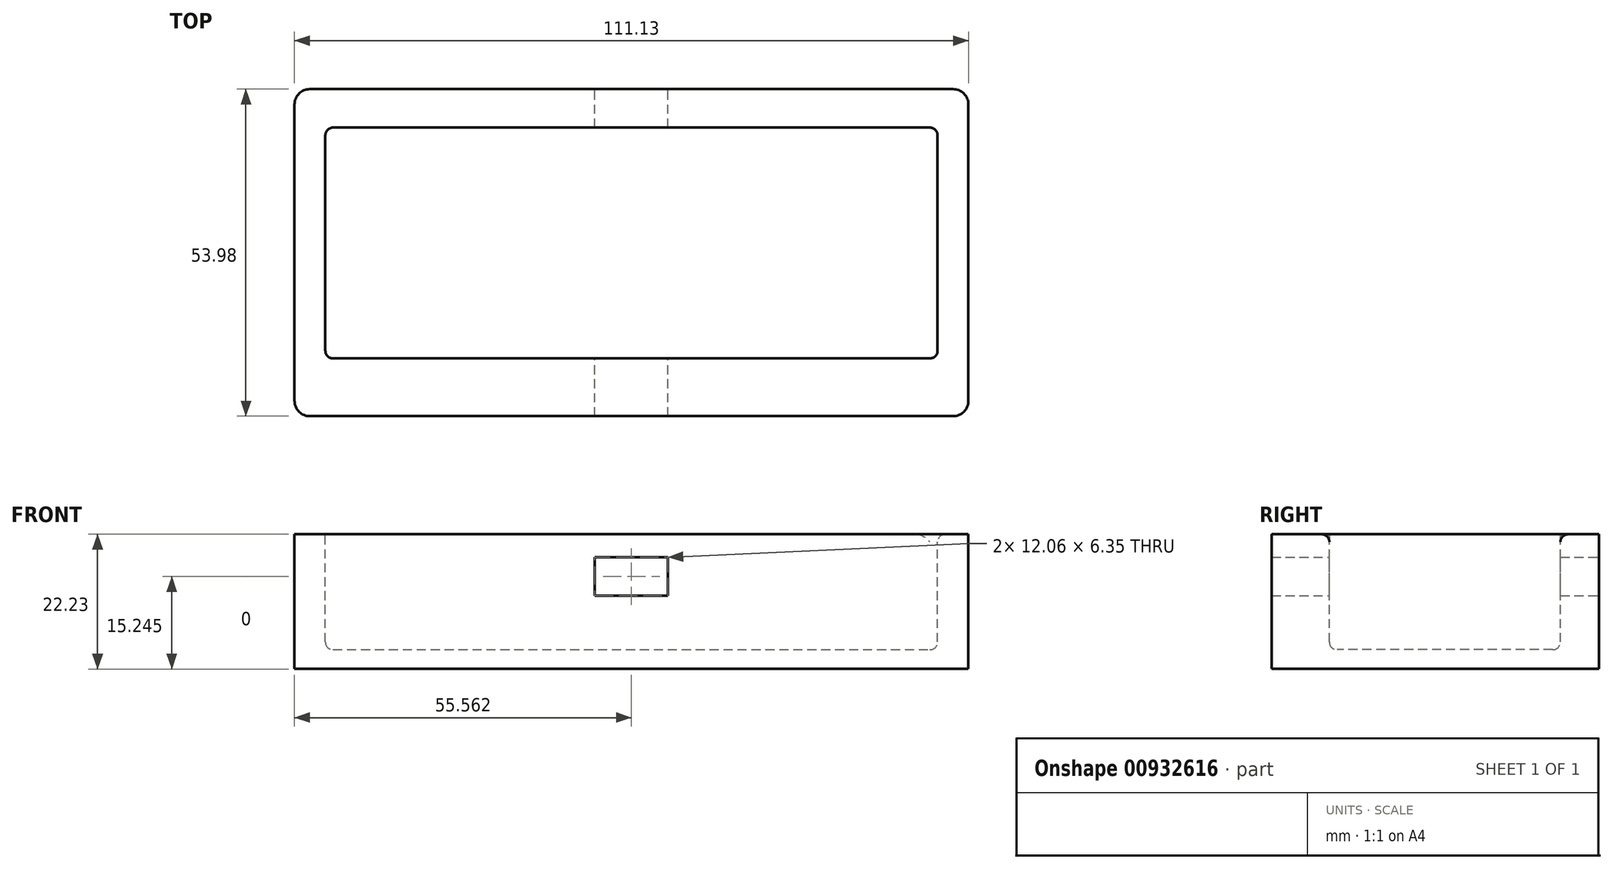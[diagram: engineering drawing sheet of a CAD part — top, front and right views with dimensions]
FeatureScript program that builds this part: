
annotation { "Feature Type Name" : "Feature", "Feature Type Description" : "" }
export const myFeature = defineFeature(function(context is Context, id is Id, definition is map)
    precondition{}
    {
        {
            var Q0;
            Q0=qCreatedBy(makeId("Top.planeOp"),FACE);
            var sketch = newSketch(context, id + "F0", { "sketchPlane" : qUnion([Q0])});
            skLineSegment(sketch, "E0.bottom", {"start": v(2.54, 0) * mm, "end": v(108.59, 0) * mm});
            skLineSegment(sketch, "E0.top", {"start": v(2.54, 53.98) * mm, "end": v(108.59, 53.98) * mm});
            skLineSegment(sketch, "E0.left", {"start": v(0, 2.54) * mm, "end": v(0, 51.44) * mm});
            skLineSegment(sketch, "E0.right", {"start": v(111.12, 2.54) * mm, "end": v(111.12, 51.44) * mm});
            skPoint(sketch, "E1.visualSharp", {"position": v(0, 53.98) * mm});
            skArc(sketch, "E1.filletArc", {"start": v(2.54, 53.98) * mm, "mid": v(0.74, 53.23) * mm, "end": v(0, 51.44) * mm});
            skPoint(sketch, "E2.visualSharp", {"position": v(111.12, 53.98) * mm});
            skArc(sketch, "E2.filletArc", {"start": v(111.12, 51.44) * mm, "mid": v(110.38, 53.23) * mm, "end": v(108.59, 53.98) * mm});
            skPoint(sketch, "E3.visualSharp", {"position": v(111.12, 0) * mm});
            skArc(sketch, "E3.filletArc", {"start": v(108.59, 0) * mm, "mid": v(110.38, 0.74) * mm, "end": v(111.13, 2.54) * mm});
            skPoint(sketch, "E4.visualSharp", {"position": v(0, 0) * mm});
            skArc(sketch, "E4.filletArc", {"start": v(0, 2.54) * mm, "mid": v(0.74, 0.74) * mm, "end": v(2.54, 0) * mm});
            skLineSegment(sketch, "E5", {"start": v(0, 26.99) * mm, "end": v(111.12, 26.99) * mm, "construction": true});
            skLineSegment(sketch, "E6", {"start": v(55.56, 53.98) * mm, "end": v(55.56, 0) * mm, "construction": true});
            skLineSegment(sketch, "E7.0", {"start": v(5.08, 47.62) * mm, "end": v(106.05, 47.62) * mm});
            skLineSegment(sketch, "E8.0", {"start": v(5.08, 9.53) * mm, "end": v(106.05, 9.53) * mm});
            skLineSegment(sketch, "E9", {"start": v(5.08, 47.62) * mm, "end": v(5.08, 9.53) * mm});
            skLineSegment(sketch, "E10", {"start": v(106.05, 47.62) * mm, "end": v(106.05, 9.53) * mm});
            skSolve(sketch);
        }
        {
            var Q0;
            Q0=makeQuery(id+"F0.imprint","IMPRINT",FACE,{"disambiguationData":[TD([[makeQuery(id+"F0.imprint","IMPRINT",EDGE,{"derivedFrom":sQuery(id+"F0.wireOp",EDGE,"E0.bottom")}),1.0]])]});
            extrude(context, id + "F1", {"entities" : qUnion([Q0]), "oppositeDirection" : true, "depth" : 19.05 * mm, "offsetDistance" : 25.4 * mm});
        }
        {
            var Q0;
            Q0=makeQuery(id+"F1.opExtrude","CAP_FACE",FACE,{"disambiguationData":[OSD([sQuery(id+"F0.wireOp",EDGE,"E0.bottom"),sQuery(id+"F0.wireOp",EDGE,"E0.top"),sQuery(id+"F0.wireOp",EDGE,"E0.left"),sQuery(id+"F0.wireOp",EDGE,"E0.right"),sQuery(id+"F0.wireOp",EDGE,"E1.filletArc"),sQuery(id+"F0.wireOp",EDGE,"E2.filletArc"),sQuery(id+"F0.wireOp",EDGE,"E3.filletArc"),sQuery(id+"F0.wireOp",EDGE,"E4.filletArc"),sQuery(id+"F0.wireOp",EDGE,"E7.0"),sQuery(id+"F0.wireOp",EDGE,"E8.0"),sQuery(id+"F0.wireOp",EDGE,"E9"),sQuery(id+"F0.wireOp",EDGE,"E10")])],"isStart":false});
            var sketch = newSketch(context, id + "F2", { "sketchPlane" : qUnion([Q0])});
            skLineSegment(sketch, "E11.0", {"start": v(2.54, -53.98) * mm, "end": v(108.59, -53.98) * mm});
            skLineSegment(sketch, "E11.1", {"start": v(111.12, -2.54) * mm, "end": v(111.12, -51.44) * mm});
            skLineSegment(sketch, "E11.2", {"start": v(0, -26.99) * mm, "end": v(111.12, -26.99) * mm});
            skLineSegment(sketch, "E11.3", {"start": v(5.08, -47.62) * mm, "end": v(106.05, -47.62) * mm});
            skLineSegment(sketch, "E11.4", {"start": v(106.05, -47.62) * mm, "end": v(106.05, -9.53) * mm});
            skLineSegment(sketch, "E11.5", {"start": v(2.54, 0) * mm, "end": v(108.59, 0) * mm});
            skLineSegment(sketch, "E11.6", {"start": v(5.08, -47.62) * mm, "end": v(5.08, -9.53) * mm});
            skLineSegment(sketch, "E11.7", {"start": v(5.08, -9.53) * mm, "end": v(106.05, -9.53) * mm});
            skLineSegment(sketch, "E11.8", {"start": v(0, -2.54) * mm, "end": v(0, -51.44) * mm});
            skLineSegment(sketch, "E11.9", {"start": v(55.56, -53.98) * mm, "end": v(55.56, 0) * mm});
            skArc(sketch, "E11.10", {"start": v(108.59, 0) * mm, "mid": v(110.38, -0.74) * mm, "end": v(111.13, -2.54) * mm});
            skArc(sketch, "E12.0.1", {"start": v(108.59, -53.97) * mm, "mid": v(110.38, -53.23) * mm, "end": v(111.13, -51.44) * mm});
            skLineSegment(sketch, "E12.0.2", {"start": v(111.12, -51.44) * mm, "end": v(111.12, -2.54) * mm});
            skArc(sketch, "E12.0.3", {"start": v(111.13, -2.54) * mm, "mid": v(110.38, -0.74) * mm, "end": v(108.59, 0) * mm});
            skLineSegment(sketch, "E12.0.4", {"start": v(108.59, 0) * mm, "end": v(2.54, 0) * mm});
            skArc(sketch, "E12.0.5", {"start": v(2.54, 0) * mm, "mid": v(0.74, -0.74) * mm, "end": v(0, -2.54) * mm});
            skArc(sketch, "E12.0.7", {"start": v(0, -51.44) * mm, "mid": v(0.74, -53.23) * mm, "end": v(2.54, -53.98) * mm});
            skLineSegment(sketch, "E13.0.2", {"start": v(106.05, -9.53) * mm, "end": v(106.05, -47.62) * mm});
            skLineSegment(sketch, "E13.0.3", {"start": v(106.05, -47.62) * mm, "end": v(5.08, -47.62) * mm});
            skSolve(sketch);
        }
        {
            var Q0;
            Q0 = qSketchRegion(id + "F2", true);
            var Q1;
            {var subQ0=sQuery(id+"F2.wireOp",EDGE,"E11.6");var subQ1=sQuery(id+"F2.wireOp",EDGE,"E11.2");var subQ2=makeQuery(id+"F2.imprint","INTERSECT",VERTEX,{"derivedFrom":[subQ1,subQ0]});Q1=makeQuery(id+"F2.imprint","IMPRINT",FACE,{"disambiguationData":[TD([[makeQuery(id+"F2.imprint","IMPRINT",EDGE,{"disambiguationData":[TD([[subQ2,-1.0]])],"derivedFrom":subQ1}),-1.0]])]});}
            var Q2;
            {var subQ0=sQuery(id+"F2.wireOp",EDGE,"E11.6");var subQ1=sQuery(id+"F2.wireOp",EDGE,"E11.2");var subQ2=makeQuery(id+"F2.imprint","INTERSECT",VERTEX,{"derivedFrom":[subQ1,subQ0]});Q2=makeQuery(id+"F2.imprint","IMPRINT",FACE,{"disambiguationData":[TD([[makeQuery(id+"F2.imprint","IMPRINT",EDGE,{"disambiguationData":[TD([[subQ2,-1.0]])],"derivedFrom":subQ1}),1.0]])]});}
            var Q3;
            {var subQ0=sQuery(id+"F2.wireOp",EDGE,"E11.9");var subQ1=sQuery(id+"F2.wireOp",EDGE,"E11.2");var subQ2=makeQuery(id+"F2.imprint","INTERSECT",VERTEX,{"derivedFrom":[subQ1,subQ0]});Q3=makeQuery(id+"F2.imprint","IMPRINT",FACE,{"disambiguationData":[TD([[makeQuery(id+"F2.imprint","IMPRINT",EDGE,{"disambiguationData":[TD([[subQ2,-1.0]])],"derivedFrom":subQ1}),1.0]])]});}
            var Q4;
            {var subQ0=sQuery(id+"F2.wireOp",EDGE,"E11.9");var subQ1=sQuery(id+"F2.wireOp",EDGE,"E11.2");var subQ2=makeQuery(id+"F2.imprint","INTERSECT",VERTEX,{"derivedFrom":[subQ1,subQ0]});Q4=makeQuery(id+"F2.imprint","IMPRINT",FACE,{"disambiguationData":[TD([[makeQuery(id+"F2.imprint","IMPRINT",EDGE,{"disambiguationData":[TD([[subQ2,-1.0]])],"derivedFrom":subQ1}),-1.0]])]});}
            extrude(context, id + "F3", {"entities" : qUnion([Q0, Q1, Q2, Q3, Q4]), "operationType" : NewBodyOperationType.ADD, "depth" : 3.17 * mm, "offsetDistance" : 25.4 * mm});
        }
        {
            var Q0;
            Q0=makeQuery(id+"F3.boolean.opBoolean","MERGE",FACE,{"derivedFrom":[makeQuery(id+"F1.opExtrude","SWEPT_FACE",FACE,{"disambiguationData":[OSD([sQuery(id+"F0.wireOp",EDGE,"E0.top")])]}),makeQuery(id+"F3.opExtrude","SWEPT_FACE",FACE,{"disambiguationData":[OSD([sQuery(id+"F2.wireOp",EDGE,"E11.0")])]})]});
            var sketch = newSketch(context, id + "F4", { "sketchPlane" : qUnion([Q0])});
            skLineSegment(sketch, "E14.bottom", {"start": v(-61.6, -3.81) * mm, "end": v(-49.53, -3.8) * mm});
            skLineSegment(sketch, "E14.top", {"start": v(-61.6, -10.16) * mm, "end": v(-49.53, -10.16) * mm});
            skLineSegment(sketch, "E14.left", {"start": v(-61.6, -3.81) * mm, "end": v(-61.6, -10.16) * mm});
            skLineSegment(sketch, "E14.right", {"start": v(-49.53, -3.8) * mm, "end": v(-49.53, -10.16) * mm});
            skSolve(sketch);
        }
        {
            var Q0;
            Q0=makeQuery(id+"F4.imprint","IMPRINT",FACE,{"disambiguationData":[TD([[makeQuery(id+"F4.imprint","IMPRINT",EDGE,{"derivedFrom":sQuery(id+"F4.wireOp",EDGE,"E14.bottom")}),-1.0]])]});
            extrude(context, id + "F5", {"entities" : qUnion([Q0]), "operationType" : NewBodyOperationType.REMOVE, "endBound" : BoundingType.THROUGH_ALL, "oppositeDirection" : true, "depth" : 25.4 * mm, "offsetDistance" : 25.4 * mm});
        }
        {
            var Q0;
            Q0=makeQuery(id+"F1.opExtrude","SWEPT_EDGE",EDGE,{"disambiguationData":[OSD([sQuery(id+"F0.wireOp",EDGE,"E7.0"),sQuery(id+"F0.wireOp",EDGE,"E9")])]});
            var Q1;
            Q1=makeQuery(id+"F1.opExtrude","SWEPT_EDGE",EDGE,{"disambiguationData":[OSD([sQuery(id+"F0.wireOp",EDGE,"E7.0"),sQuery(id+"F0.wireOp",EDGE,"E10")])]});
            var Q2;
            Q2=makeQuery(id+"F1.opExtrude","SWEPT_EDGE",EDGE,{"disambiguationData":[OSD([sQuery(id+"F0.wireOp",EDGE,"E8.0"),sQuery(id+"F0.wireOp",EDGE,"E9")])]});
            var Q3;
            Q3=makeQuery(id+"F1.opExtrude","SWEPT_EDGE",EDGE,{"disambiguationData":[OSD([sQuery(id+"F0.wireOp",EDGE,"E8.0"),sQuery(id+"F0.wireOp",EDGE,"E10")])]});
            var Q4;
            Q4=makeQuery(id+"F3.opExtrude","CAP_FACE",FACE,{"disambiguationData":[OSD([sQuery(id+"F2.wireOp",EDGE,"E11.0"),sQuery(id+"F2.wireOp",EDGE,"E12.0.1"),sQuery(id+"F2.wireOp",EDGE,"E12.0.2"),sQuery(id+"F2.wireOp",EDGE,"E12.0.3"),sQuery(id+"F2.wireOp",EDGE,"E12.0.5"),sQuery(id+"F2.wireOp",EDGE,"E11.8"),sQuery(id+"F2.wireOp",EDGE,"E12.0.7"),sQuery(id+"F2.wireOp",EDGE,"E11.5")])],"isStart":true});
            var Q5;
            Q5=makeQuery(id+"F1.opExtrude","CAP_EDGE",EDGE,{"disambiguationData":[OSD([sQuery(id+"F0.wireOp",EDGE,"E10")])],"isStart":true});
            fillet(context, id + "F6", {"entities" : qUnion([Q0, Q1, Q2, Q3, Q4, Q5]), "radius" : 1.27 * mm, "tangentPropagation" : true, "allowEdgeOverflow" : false});
        }
    });
